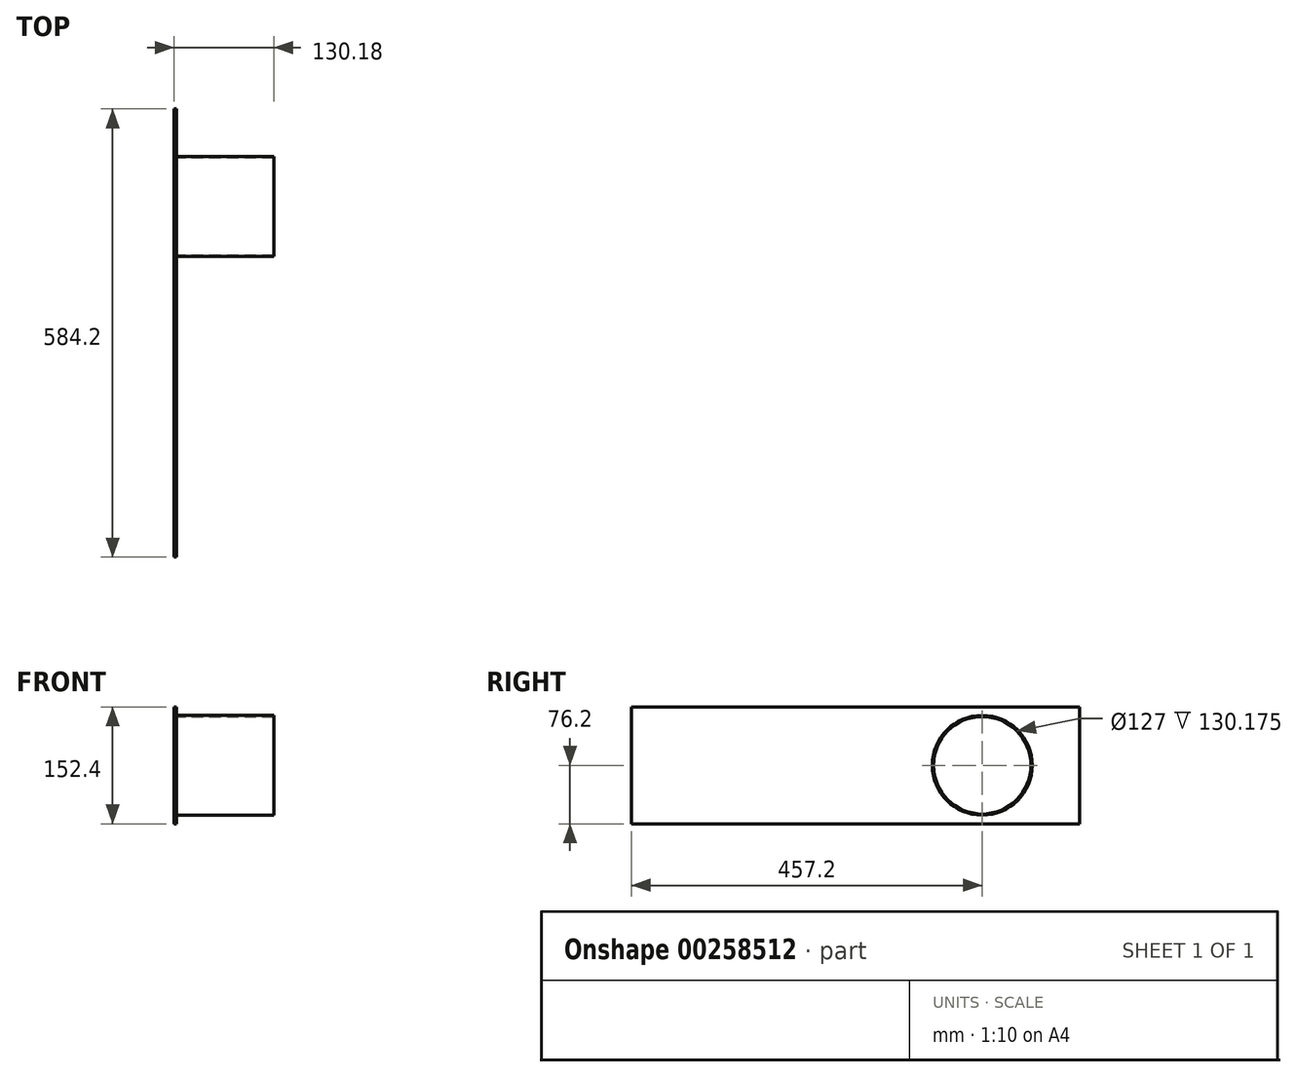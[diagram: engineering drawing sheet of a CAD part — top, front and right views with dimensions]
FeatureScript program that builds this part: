
annotation { "Feature Type Name" : "Feature", "Feature Type Description" : "" }
export const myFeature = defineFeature(function(context is Context, id is Id, definition is map)
    precondition{}
    {
        {
            var Q0;
            Q0=qCreatedBy(makeId("Right.planeOp"),FACE);
            var sketch = newSketch(context, id + "F0", { "sketchPlane" : qUnion([Q0])});
            skLineSegment(sketch, "E0.bottom", {"start": v(292.1, 76.2) * mm, "end": v(-292.1, 76.2) * mm});
            skLineSegment(sketch, "E0.top", {"start": v(292.1, -76.2) * mm, "end": v(-292.1, -76.2) * mm});
            skLineSegment(sketch, "E0.left", {"start": v(292.1, 76.2) * mm, "end": v(292.1, -76.2) * mm});
            skLineSegment(sketch, "E0.right", {"start": v(-292.1, 76.2) * mm, "end": v(-292.1, -76.2) * mm});
            skPoint(sketch, "E0.middle", {"position": v(0, 0) * mm});
            skSolve(sketch);
        }
        {
            var Q0;
            Q0 = qSketchRegion(id + "F0", true);
            extrude(context, id + "F1", {"entities" : qUnion([Q0]), "depth" : 3.17 * mm});
        }
        {
            var Q0;
            Q0=makeQuery(id+"F1.opExtrude","CAP_FACE",FACE,{"disambiguationData":[OSD([sQuery(id+"F0.wireOp",EDGE,"E0.bottom"),sQuery(id+"F0.wireOp",EDGE,"E0.top"),sQuery(id+"F0.wireOp",EDGE,"E0.left"),sQuery(id+"F0.wireOp",EDGE,"E0.right")])],"isStart":false});
            var sketch = newSketch(context, id + "F2", { "sketchPlane" : qUnion([Q0])});
            skCircle(sketch, "E1", {"center": v(165.1, 0) * mm, "radius": 63.5 * mm});
            skSolve(sketch);
        }
        {
            var Q0;
            Q0 = qSketchRegion(id + "F2", true);
            extrude(context, id + "F3", {"entities" : qUnion([Q0]), "operationType" : NewBodyOperationType.REMOVE, "oppositeDirection" : true, "depth" : 25.4 * mm});
        }
        {
            var Q0;
            Q0=makeQuery(id+"F1.opExtrude","CAP_FACE",FACE,{"disambiguationData":[OSD([sQuery(id+"F0.wireOp",EDGE,"E0.bottom"),sQuery(id+"F0.wireOp",EDGE,"E0.top"),sQuery(id+"F0.wireOp",EDGE,"E0.left"),sQuery(id+"F0.wireOp",EDGE,"E0.right")])],"isStart":false});
            var sketch = newSketch(context, id + "F4", { "sketchPlane" : qUnion([Q0])});
            skCircle(sketch, "E2", {"center": v(165.1, 0) * mm, "radius": 63.5 * mm});
            skCircle(sketch, "E3", {"center": v(165.1, 0) * mm, "radius": 65.09 * mm});
            skSolve(sketch);
        }
        {
            var Q0;
            Q0 = qSketchRegion(id + "F4", true);
            extrude(context, id + "F5", {"entities" : qUnion([Q0]), "operationType" : NewBodyOperationType.ADD, "depth" : 127 * mm});
        }
    });
